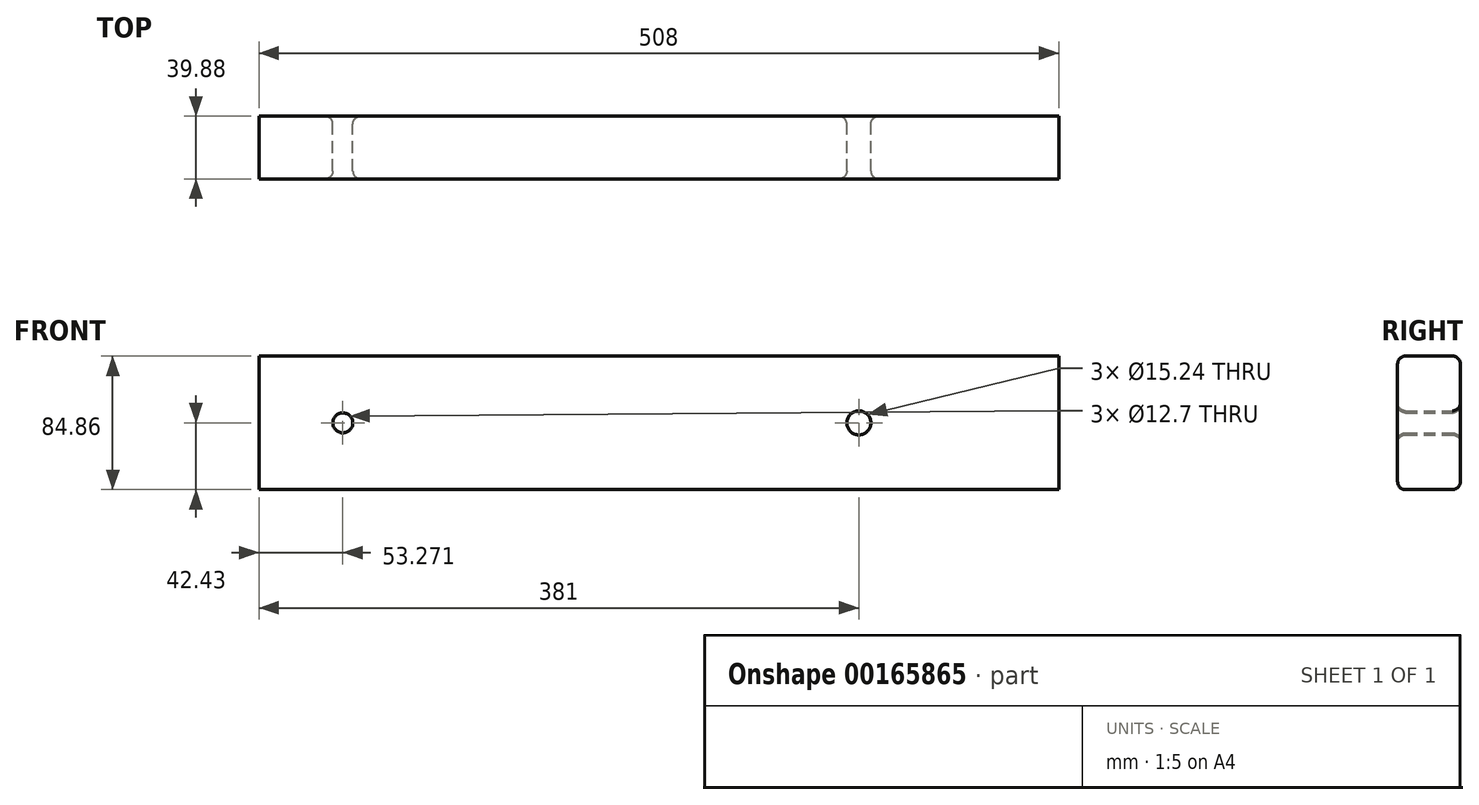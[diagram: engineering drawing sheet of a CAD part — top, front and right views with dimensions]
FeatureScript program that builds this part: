
annotation { "Feature Type Name" : "Feature", "Feature Type Description" : "" }
export const myFeature = defineFeature(function(context is Context, id is Id, definition is map)
    precondition{}
    {
        {
            var Q0;
            Q0=qCreatedBy(makeId("Front.planeOp"),FACE);
            var sketch = newSketch(context, id + "F0", { "sketchPlane" : qUnion([Q0])});
            skLineSegment(sketch, "E0.bottom", {"start": v(254, -42.43) * mm, "end": v(-254, -42.43) * mm});
            skLineSegment(sketch, "E0.top", {"start": v(254, 42.43) * mm, "end": v(-254, 42.43) * mm});
            skLineSegment(sketch, "E0.left", {"start": v(254, -42.43) * mm, "end": v(254, 42.43) * mm});
            skLineSegment(sketch, "E0.right", {"start": v(-254, -42.43) * mm, "end": v(-254, 42.43) * mm});
            skPoint(sketch, "E0.middle", {"position": v(0, 0) * mm});
            skLineSegment(sketch, "E1", {"start": v(254, 42.43) * mm, "end": v(127, 42.43) * mm});
            skCircle(sketch, "E2", {"center": v(127, 0) * mm, "radius": 7.62 * mm});
            skLineSegment(sketch, "E3", {"start": v(-254, 42.43) * mm, "end": v(-200.73, 42.43) * mm});
            skCircle(sketch, "E4", {"center": v(-200.73, 0) * mm, "radius": 6.35 * mm});
            skSolve(sketch);
        }
        {
            var Q0;
            Q0 = qSketchRegion(id + "F0", true);
            extrude(context, id + "F1", {"entities" : qUnion([Q0]), "depth" : 39.88 * mm});
        }
        {
            var Q0;
            Q0=makeQuery(id+"F1.opExtrude","CAP_EDGE",EDGE,{"disambiguationData":[OSD([sQuery(id+"F0.wireOp",EDGE,"E0.top"),sQuery(id+"F0.wireOp",EDGE,"E1"),sQuery(id+"F0.wireOp",EDGE,"E3")])],"isStart":true});
            var Q1;
            Q1=makeQuery(id+"F1.opExtrude","CAP_EDGE",EDGE,{"disambiguationData":[OSD([sQuery(id+"F0.wireOp",EDGE,"E0.bottom")])],"isStart":true});
            var Q2;
            Q2=makeQuery(id+"F1.opExtrude","CAP_EDGE",EDGE,{"disambiguationData":[OSD([sQuery(id+"F0.wireOp",EDGE,"E2")])],"isStart":true});
            var Q3;
            Q3=makeQuery(id+"F1.opExtrude","CAP_EDGE",EDGE,{"disambiguationData":[OSD([sQuery(id+"F0.wireOp",EDGE,"E4")])],"isStart":true});
            var Q4;
            Q4=makeQuery(id+"F1.opExtrude","CAP_EDGE",EDGE,{"disambiguationData":[OSD([sQuery(id+"F0.wireOp",EDGE,"E0.top"),sQuery(id+"F0.wireOp",EDGE,"E1"),sQuery(id+"F0.wireOp",EDGE,"E3")])],"isStart":false});
            var Q5;
            Q5=makeQuery(id+"F1.opExtrude","CAP_EDGE",EDGE,{"disambiguationData":[OSD([sQuery(id+"F0.wireOp",EDGE,"E0.bottom")])],"isStart":false});
            var Q6;
            Q6=makeQuery(id+"F1.opExtrude","CAP_EDGE",EDGE,{"disambiguationData":[OSD([sQuery(id+"F0.wireOp",EDGE,"E4")])],"isStart":false});
            var Q7;
            Q7=makeQuery(id+"F1.opExtrude","CAP_EDGE",EDGE,{"disambiguationData":[OSD([sQuery(id+"F0.wireOp",EDGE,"E2")])],"isStart":false});
            fillet(context, id + "F2", {"entities" : qUnion([Q0, Q1, Q2, Q3, Q4, Q5, Q6, Q7]), "radius" : 5.08 * mm, "tangentPropagation" : true, "allowEdgeOverflow" : false});
        }
    });
